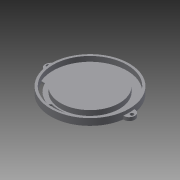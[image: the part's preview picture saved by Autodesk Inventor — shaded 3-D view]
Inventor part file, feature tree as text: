
AUTODESK INVENTOR PART (.ipt)
format: ipt  version: 2015 SP2 (Build 190223200, 223)  size: 194,560 bytes
history: native  units: in
note: dims shown in document units (in); Inventor stores cm internally (conversion verified against a paired STEP export)
features: sketch x13, extrude x11, hole x2
ambient origin geometry x8: Origin, YZ Plane, XZ Plane, XY Plane, X Axis, Y Axis, Z Axis, Center Point
bodies: Solid1 (feature_tree)
feature tree (26):
  extrude  "Extrusion1"  Depth=2.5984in
  extrude  "Extrusion2"  Depth=0.0591in
  extrude  "Extrusion3"  TaperAngle=45.0deg  [1 undecoded]
  extrude  "Extrusion4"  Depth=0.2953in
  extrude  "Extrusion5"  Depth=0.0591in TaperAngle=0.0deg
  extrude  "Extrusion6"  TaperAngle=180.0deg  [1 undecoded]
  extrude  "Extrusion7"  Depth=0.0591in TaperAngle=0.0deg
  extrude  "Extrusion8"  Depth=0.1969in TaperAngle=0.0deg
  extrude  "Extrusion9"  Depth=2.0669in
  extrude  "Extrusion10"  Depth=0.1378in TaperAngle=0.0deg
  hole  "Hole1"  [1 undecoded]
  hole  "Hole2"  [1 undecoded]
  extrude  "Extrusion11"  Depth=0.3937in
  sketch  "Sketch1"  dims[d0=2.0669in d1=2.5984in]
  sketch  "Sketch2"  dims[d2=0.0591in d3=0.0in d4=2.1654in]
  sketch  "Sketch3"  dims[d5=135.0deg d6=45.0deg]
  sketch  "Sketch4"  dims[d7=0.5906in d9=0.2953in]
  sketch  "Sketch5"  dims[d10=0.0in d11=0.0591in d12=0.0in]
  sketch  "Sketch6"  dims[d13=2.3622in d14=180.0deg]
  sketch  "Sketch7"  dims[d15=0.3937in d16=0.0in d17=0.0591in d18=0.0in]
  sketch  "Sketch8"  dims[d19=1.7717in d20=0.1969in d21=0.0in]
  sketch  "Sketch9"  dims[d22=1.7717in d23=2.0669in]
  sketch  "Sketch10"  dims[d24=2.0669in d25=0.1378in d26=0.0in]
  sketch  "Sketch11"  dims[d27=0.0394in d28=0.0in d29=2.5984in]
  sketch  "Sketch13"  dims[d30=0.0787in d31=0.2362in d32=0.0in]
  sketch  "Sketch14"  dims[d33=0.3937in d34=0.3937in d35=0.1181in d36=0.0in d37=0.3937in d38=0.1181in d39=0.0in d40=0.0984in d41=0.1181in d42=0.1181in d43=0.2362in d44=0.1575in d45=0.0787in d46=90.0deg d47=0.315in d48=0.8108in d49=0.0984in d50=0.1181in d51=0.1181in d52=0.2362in d53=0.1575in d54=0.0787in d55=90.0deg d56=0.315in d57=0.8108in d58=1.9685in d59=0.0787in d60=0.0in]
note: 4 required parameter values undecoded (feature->parameter linkage not recoverable at this tier; creation-order binding heuristic only, values carry confidence <= 0.55)
